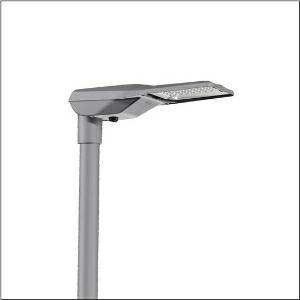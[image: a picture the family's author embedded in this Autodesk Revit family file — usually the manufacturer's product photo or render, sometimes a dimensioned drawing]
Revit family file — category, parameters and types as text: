
# Revit family: streetlight_sl_21_iq_mini___p0_8ab_5xe2r31u08jb_749f
name_source: partatom
category: Lighting Fixtures
units: mm (PartAtom-declared; Revit-internal decimal feet)

## family parameters
Cut with Voids When Loaded = No
Host = Face
Light Source = No
Part Type = Normal
Room Calculation Point = No
Round Connector Dimension = Use Diameter
Shared = No

## types (1)
- --- (1 x LED, 9740 lm, 72.5 W, 3000K)
    Apparent Load = 73 VA
    CIE Flux Codes = 39 72 97 100 100
    Color Rendering = 70
    Color Temperature = 3000K
    Default Elevation = 1800 mm
    Description = Streetlight SL 21 iQ mini, mast luminaire, primary light control with lens, of PMMA, primary optical cover: cover, of toughened safety glass, transparent, light distribution: P0.8aB, light emission: direct distribution, primary light characteristic: asymmetric, installation type: post-top, side-entry, LED, High Power LED, rated luminous flux: 9.740lm, luminous efficacy: 134lm/W, light colour: 730, colour temperature: 3000K, control gear: iQ-Street Remote, D4i with power reduction, control: pre-setting: logarithmic dimming characteristic, Street-Remote, Auto-Match, Temp-Guard, Lumen-Switch, Night-Set, Smart-Wire, Light-Fading, Desk-Remote (wireless, voltage-free reading and setting of iQ features in the workshop via application-optimized NFC function/RFID function), optimised constant luminous flux control (CLO 2.0), mains connection: 220..240V, AC, 50/60Hz, start of lifetime: 73W, end of service life: 76W, reduction: 33W, luminaire housing, of diecast aluminium, powder-coated, Siteco® metallic grey (DB 702S), corrosivity category C5 mid according to DIN EN ISO 12944, please order mast flange separately, inclination adjustable: 0°, 5°, 10°, 15°, sealing non-destructively replaceable, multi-level sealing system, length: 628mm, width: 235mm, height: 110mm, mast flange for spigot size: 42mm (side-entry): 5XC10008XM4, 60/48mm (side-entry/post-top): 5XC10108XM2, 76/60mm (side-entry/post-top): 5XC10108XM1, mounting height: 4..8m, Smart Interface below, protection rating (complete): IP66, insulation class (complete): insulation class II (safety insulation), certification: CE, ENEC, ENEC+, VDE, impact resistance: IK10, permissible operating ambient temperature for outdoor applications: -40..+50°C, standard-compliant lighting for roads and squares, packaging unit: 1 piece

Light Distribution: P0.8aB
    Height = 110 mm
    Lamp = 1 x LED
    Lamp Light Flux = 9740 lm
    Lamp Power = 72.5 W
    Lamp count = 1
    Length = 625 mm
    Luminous efficacy = 134 lm/W
    Manufacturer = Siteco
    ModVariant = No
    Model = 5XE2R31U08JB
    Number of Poles = 1
    OnlyDefault = Yes
    Power Factor = 1
    Product Name = Streetlight SL 21 iQ mini | P0.8aB
    Product group = mast luminaire | pylon top
    ProductGroupID = 6100
    Protection Class = Protection class II
    Protection Degree = IP 66
    RLX_Detail_Level = 1
    RLX_Emergency_Light_Flux = 0 lm
    RLX_Emergency_Type = 0
    RLX_Emergency_Type_DB = No
    RlxData = <blob elided: 26221 chars, md5=a144cf5e>
    Socket = socket
    Standby Power = 0 W
    System Light Flux = 9740 lm
    System Power = 73 W
    Type Comments = factory setting: luminous flux: 100 % | dim-lin: 254 | 755 mA
    Type Image = l_1003516.jpg
    URL = http://relux.com
    VarID = @adj_071364
    Voltage = 0 V
    Weight = 0.00 kg
    Width = 234 mm

## geometry (parser evidence)
native form markers: Blend x4, Sweep x10
no freeform markers — native parametric forms only
